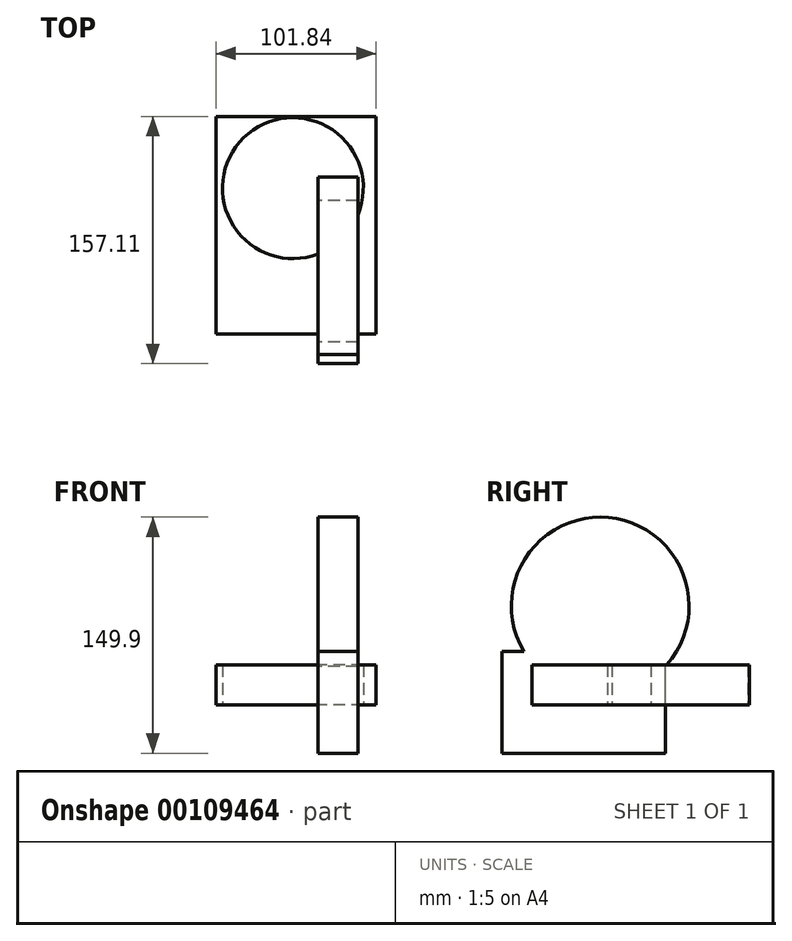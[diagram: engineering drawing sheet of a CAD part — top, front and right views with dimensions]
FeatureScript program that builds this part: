
annotation { "Feature Type Name" : "Feature", "Feature Type Description" : "" }
export const myFeature = defineFeature(function(context is Context, id is Id, definition is map)
    precondition{}
    {
        {
            var Q0;
            Q0=qCreatedBy(makeId("Top.planeOp"),FACE);
            var sketch = newSketch(context, id + "F0", { "sketchPlane" : qUnion([Q0])});
            skCircle(sketch, "E0", {"center": v(-15.97, 12.92) * mm, "radius": 44.74 * mm});
            skLineSegment(sketch, "E1.bottom", {"start": v(36.96, -79.64) * mm, "end": v(-64.88, -79.64) * mm});
            skLineSegment(sketch, "E1.top", {"start": v(36.96, 58.55) * mm, "end": v(-64.88, 58.55) * mm});
            skLineSegment(sketch, "E1.left", {"start": v(36.96, -79.64) * mm, "end": v(36.96, 58.55) * mm});
            skLineSegment(sketch, "E1.right", {"start": v(-64.88, -79.64) * mm, "end": v(-64.88, 58.55) * mm});
            skSolve(sketch);
        }
        {
            var Q0;
            Q0=qCreatedBy(makeId("Right.planeOp"),FACE);
            var sketch = newSketch(context, id + "F1", { "sketchPlane" : qUnion([Q0])});
            skCircle(sketch, "E2", {"center": v(-36.31, 62.86) * mm, "radius": 56.42 * mm});
            skLineSegment(sketch, "E3.bottom", {"start": v(5.19, -30.62) * mm, "end": v(-98.56, -30.62) * mm});
            skLineSegment(sketch, "E3.top", {"start": v(5.19, 34.1) * mm, "end": v(-98.56, 34.1) * mm});
            skLineSegment(sketch, "E3.left", {"start": v(5.19, -30.62) * mm, "end": v(5.19, 34.1) * mm});
            skLineSegment(sketch, "E3.right", {"start": v(-98.56, -30.62) * mm, "end": v(-98.56, 34.1) * mm});
            skSolve(sketch);
        }
        {
            var Q0;
            Q0 = qSketchRegion(id + "F1", true);
            extrude(context, id + "F2", {"entities" : qUnion([Q0]), "depth" : 25.4 * mm});
        }
        {
            var Q0;
            Q0 = qSketchRegion(id + "F0", true);
            extrude(context, id + "F3", {"entities" : qUnion([Q0]), "operationType" : NewBodyOperationType.ADD, "depth" : 25.4 * mm});
        }
    });
